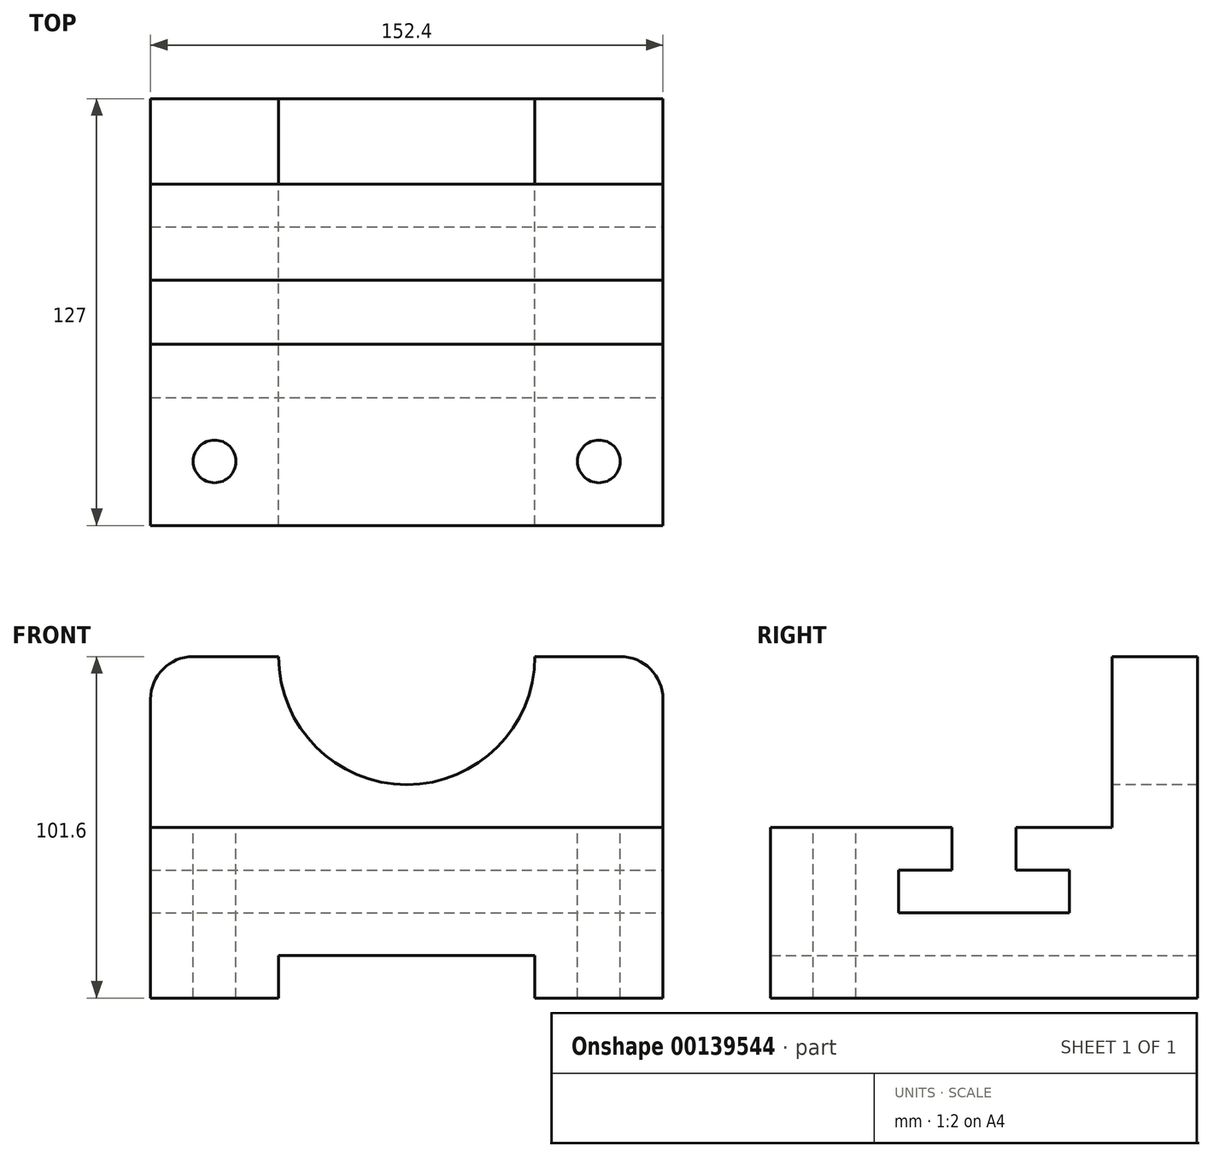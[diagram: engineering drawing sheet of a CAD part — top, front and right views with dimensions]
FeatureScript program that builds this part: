
annotation { "Feature Type Name" : "Feature", "Feature Type Description" : "" }
export const myFeature = defineFeature(function(context is Context, id is Id, definition is map)
    precondition{}
    {
        {
            var Q0;
            Q0=qCreatedBy(makeId("Front.planeOp"),FACE);
            var sketch = newSketch(context, id + "F0", { "sketchPlane" : qUnion([Q0])});
            skLineSegment(sketch, "E0", {"start": v(-48.09, 0) * mm, "end": v(-9.99, 0) * mm});
            skLineSegment(sketch, "E1", {"start": v(-9.99, 0) * mm, "end": v(-9.99, 12.7) * mm});
            skLineSegment(sketch, "E2", {"start": v(-9.99, 12.7) * mm, "end": v(66.21, 12.7) * mm});
            skLineSegment(sketch, "E3", {"start": v(66.21, 12.7) * mm, "end": v(66.21, 0) * mm});
            skLineSegment(sketch, "E4", {"start": v(66.21, 0) * mm, "end": v(104.31, 0) * mm});
            skLineSegment(sketch, "E5", {"start": v(104.31, 0) * mm, "end": v(104.31, 50.8) * mm});
            skLineSegment(sketch, "E6", {"start": v(-48.09, 0) * mm, "end": v(-48.09, 50.8) * mm});
            skLineSegment(sketch, "E7", {"start": v(-48.09, 50.8) * mm, "end": v(104.31, 50.8) * mm});
            skSolve(sketch);
        }
        {
            var Q0;
            Q0=makeQuery(id+"F0.imprint","IMPRINT",FACE,{"disambiguationData":[TD([[makeQuery(id+"F0.imprint","IMPRINT",EDGE,{"derivedFrom":sQuery(id+"F0.wireOp",EDGE,"E0")}),1.0]])]});
            extrude(context, id + "F1", {"entities" : qUnion([Q0]), "depth" : 101.6 * mm});
        }
        {
            var Q0;
            Q0=makeQuery(id+"F1.opExtrude","SWEPT_FACE",FACE,{"disambiguationData":[OSD([sQuery(id+"F0.wireOp",EDGE,"E7")])]});
            var sketch = newSketch(context, id + "F2", { "sketchPlane" : qUnion([Q0])});
            skCircle(sketch, "E8", {"center": v(-29.04, -82.55) * mm, "radius": 6.35 * mm});
            skCircle(sketch, "E9", {"center": v(85.26, -82.55) * mm, "radius": 6.35 * mm});
            skSolve(sketch);
        }
        {
            var Q0;
            Q0=makeQuery(id+"F1.opExtrude","SWEPT_FACE",FACE,{"disambiguationData":[OSD([sQuery(id+"F0.wireOp",EDGE,"E5")])]});
            var sketch = newSketch(context, id + "F3", { "sketchPlane" : qUnion([Q0])});
            skLineSegment(sketch, "E10", {"start": v(-47.62, 50.8) * mm, "end": v(-47.62, 38.1) * mm});
            skLineSegment(sketch, "E11", {"start": v(-47.62, 38.1) * mm, "end": v(-63.5, 38.1) * mm});
            skLineSegment(sketch, "E12", {"start": v(-63.5, 38.1) * mm, "end": v(-63.5, 25.4) * mm});
            skLineSegment(sketch, "E13", {"start": v(-63.5, 25.4) * mm, "end": v(-12.7, 25.4) * mm});
            skLineSegment(sketch, "E14", {"start": v(-12.7, 25.4) * mm, "end": v(-12.7, 38.1) * mm});
            skLineSegment(sketch, "E15", {"start": v(-12.7, 38.1) * mm, "end": v(-28.58, 38.1) * mm});
            skLineSegment(sketch, "E16", {"start": v(-28.58, 38.1) * mm, "end": v(-28.58, 50.8) * mm});
            skSolve(sketch);
        }
        {
            var Q0;
            {var subQ0=sQuery(id+"F3.wireOp",EDGE,"E10");Q0=makeQuery(id+"F3.imprint","IMPRINT",FACE,{"disambiguationData":[TD([[makeQuery(id+"F3.imprint","IMPRINT",EDGE,{"derivedFrom":subQ0}),1.0]])]});}
            extrude(context, id + "F4", {"entities" : qUnion([Q0]), "operationType" : NewBodyOperationType.REMOVE, "oppositeDirection" : true, "depth" : 152.4 * mm});
        }
        {
            var Q0;
            Q0 = qSketchRegion(id + "F2", true);
            extrude(context, id + "F5", {"entities" : qUnion([Q0]), "operationType" : NewBodyOperationType.REMOVE, "endBound" : BoundingType.THROUGH_ALL, "oppositeDirection" : true, "depth" : 25.4 * mm});
        }
        {
            var Q0;
            Q0=makeQuery(id+"F1.opExtrude","SWEPT_FACE",FACE,{"disambiguationData":[OSD([sQuery(id+"F0.wireOp",EDGE,"E5")])]});
            var sketch = newSketch(context, id + "F6", { "sketchPlane" : qUnion([Q0])});
            skLineSegment(sketch, "E17", {"start": v(0, 50.8) * mm, "end": v(0, 101.6) * mm});
            skLineSegment(sketch, "E18", {"start": v(0, 101.6) * mm, "end": v(25.4, 101.6) * mm});
            skLineSegment(sketch, "E19", {"start": v(25.4, 101.6) * mm, "end": v(25.4, 0) * mm});
            skLineSegment(sketch, "E20", {"start": v(25.4, 0) * mm, "end": v(0, 0) * mm});
            skSolve(sketch);
        }
        {
            var Q0;
            Q0=makeQuery(id+"F6.imprint","IMPRINT",FACE,{"disambiguationData":[TD([[makeQuery(id+"F6.imprint","IMPRINT",EDGE,{"derivedFrom":sQuery(id+"F6.wireOp",EDGE,"E17")}),-1.0]])]});
            extrude(context, id + "F7", {"entities" : qUnion([Q0]), "operationType" : NewBodyOperationType.ADD, "oppositeDirection" : true, "depth" : 152.4 * mm});
        }
        {
            var Q0;
            Q0=makeQuery(id+"F7.opExtrude","CAP_EDGE",EDGE,{"disambiguationData":[OSD([sQuery(id+"F6.wireOp",EDGE,"E18")])],"isStart":true});
            var Q1;
            Q1=makeQuery(id+"F7.opExtrude","CAP_EDGE",EDGE,{"disambiguationData":[OSD([sQuery(id+"F6.wireOp",EDGE,"E18")])],"isStart":false});
            fillet(context, id + "F8", {"entities" : qUnion([Q0, Q1]), "radius" : 12.7 * mm, "tangentPropagation" : true, "allowEdgeOverflow" : false});
        }
        {
            var Q0;
            {var subQ3=sQuery(id+"F6.wireOp",EDGE,"E17");var subQ4=sQuery(id+"F0.wireOp",EDGE,"E5");Q0=makeQuery(id+"F7.boolean.opBoolean","SPLIT",FACE,{"disambiguationData":[TD([makeQuery(id+"F1.opExtrude","SWEPT_FACE",FACE,{"disambiguationData":[OSD([subQ4])]})])],"derivedFrom":makeQuery(id+"F7.opExtrude","SWEPT_FACE",FACE,{"disambiguationData":[OSD([subQ4,subQ3])]})});}
            var sketch = newSketch(context, id + "F9", { "sketchPlane" : qUnion([Q0])});
            skCircle(sketch, "E21", {"center": v(28.11, 101.6) * mm, "radius": 38.1 * mm});
            skSolve(sketch);
        }
        {
            var Q0;
            Q0 = qSketchRegion(id + "F9", true);
            extrude(context, id + "F10", {"entities" : qUnion([Q0]), "operationType" : NewBodyOperationType.REMOVE, "oppositeDirection" : true, "depth" : 25.4 * mm});
        }
        {
            var Q0;
            Q0=makeQuery(id+"F7.opExtrude","SWEPT_FACE",FACE,{"disambiguationData":[OSD([sQuery(id+"F6.wireOp",EDGE,"E19")])]});
            var sketch = newSketch(context, id + "F11", { "sketchPlane" : qUnion([Q0])});
            skLineSegment(sketch, "E22.0", {"start": v(9.99, 12.7) * mm, "end": v(-66.21, 12.7) * mm});
            skLineSegment(sketch, "E23.0", {"start": v(-66.21, 12.7) * mm, "end": v(-66.21, 0) * mm});
            skLineSegment(sketch, "E24.0", {"start": v(9.99, 0) * mm, "end": v(9.99, 12.7) * mm});
            skLineSegment(sketch, "E25", {"start": v(-66.21, 0) * mm, "end": v(9.99, 0) * mm});
            skSolve(sketch);
        }
        {
            var Q0;
            Q0 = qSketchRegion(id + "F11", true);
            extrude(context, id + "F12", {"entities" : qUnion([Q0]), "operationType" : NewBodyOperationType.REMOVE, "oppositeDirection" : true, "depth" : 25.4 * mm});
        }
    });
